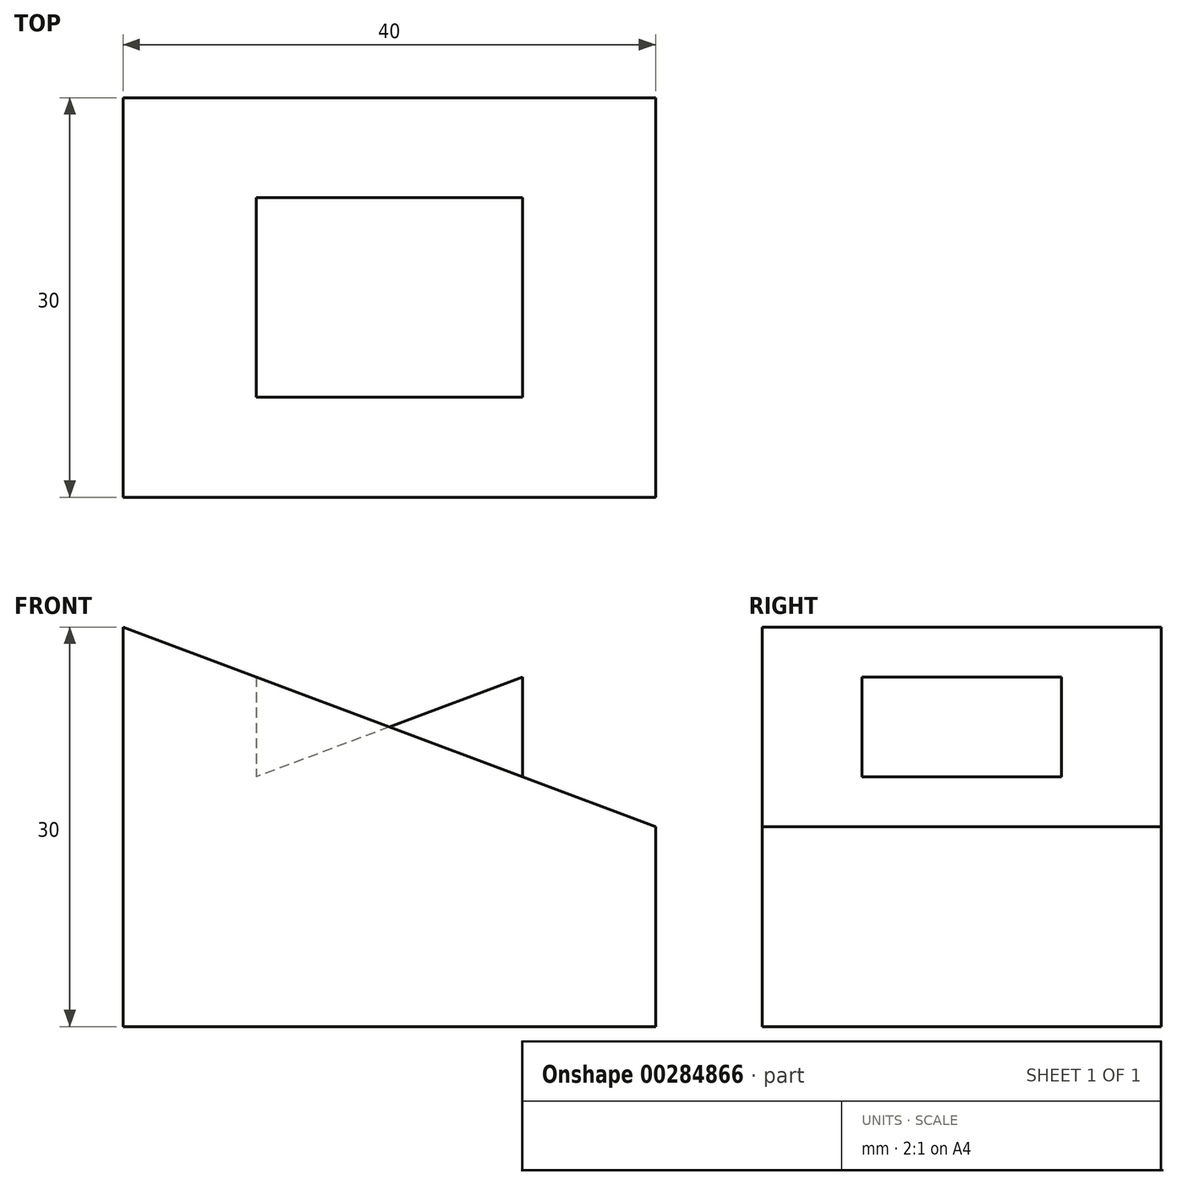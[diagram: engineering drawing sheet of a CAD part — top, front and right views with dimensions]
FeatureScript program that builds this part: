
annotation { "Feature Type Name" : "Feature", "Feature Type Description" : "" }
export const myFeature = defineFeature(function(context is Context, id is Id, definition is map)
    precondition{}
    {
        {
            var Q0;
            Q0=qCreatedBy(makeId("Front.planeOp"),FACE);
            var sketch = newSketch(context, id + "F0", { "sketchPlane" : qUnion([Q0])});
            skLineSegment(sketch, "E0.bottom", {"start": v(0, 0) * mm, "end": v(40, 0) * mm});
            skLineSegment(sketch, "E0.top", {"start": v(0, 30) * mm, "end": v(40, 30) * mm});
            skLineSegment(sketch, "E0.left", {"start": v(0, 0) * mm, "end": v(0, 30) * mm});
            skLineSegment(sketch, "E0.right", {"start": v(40, 0) * mm, "end": v(40, 30) * mm});
            skLineSegment(sketch, "E1", {"start": v(0, 30) * mm, "end": v(40, 15) * mm});
            skLineSegment(sketch, "E2.bottom", {"start": v(10, 26.25) * mm, "end": v(30, 26.25) * mm});
            skLineSegment(sketch, "E2.top", {"start": v(10, 18.75) * mm, "end": v(30, 18.75) * mm});
            skLineSegment(sketch, "E2.left", {"start": v(10, 26.25) * mm, "end": v(10, 18.75) * mm});
            skLineSegment(sketch, "E2.right", {"start": v(30, 26.25) * mm, "end": v(30, 18.75) * mm});
            skLineSegment(sketch, "E3", {"start": v(30, 26.25) * mm, "end": v(10, 18.75) * mm});
            skSolve(sketch);
        }
        {
            var Q0;
            {var subQ4=sQuery(id+"F0.wireOp",EDGE,"E0.bottom");Q0=makeQuery(id+"F0.imprint","IMPRINT",FACE,{"disambiguationData":[TD([[makeQuery(id+"F0.imprint","IMPRINT",EDGE,{"derivedFrom":subQ4}),1.0]])]});}
            var Q1;
            {var subQ2=sQuery(id+"F0.wireOp",EDGE,"E2.top");Q1=makeQuery(id+"F0.imprint","IMPRINT",FACE,{"disambiguationData":[TD([[makeQuery(id+"F0.imprint","IMPRINT",EDGE,{"derivedFrom":subQ2}),1.0]])]});}
            var Q2;
            {var subQ0=sQuery(id+"F0.wireOp",EDGE,"E2.left");Q2=makeQuery(id+"F0.imprint","IMPRINT",FACE,{"disambiguationData":[TD([[makeQuery(id+"F0.imprint","IMPRINT",EDGE,{"derivedFrom":subQ0}),1.0]])]});}
            extrude(context, id + "F1", {"entities" : qUnion([Q0, Q1, Q2]), "depth" : 30 * mm, "symmetric" : true});
        }
        {
            var Q0;
            {var subQ0=sQuery(id+"F0.wireOp",EDGE,"E2.left");Q0=makeQuery(id+"F0.imprint","IMPRINT",FACE,{"disambiguationData":[TD([[makeQuery(id+"F0.imprint","IMPRINT",EDGE,{"derivedFrom":subQ0}),1.0]])]});}
            extrude(context, id + "F2", {"entities" : qUnion([Q0]), "operationType" : NewBodyOperationType.REMOVE, "oppositeDirection" : true, "depth" : 15 * mm, "symmetric" : true});
        }
        {
            var Q0;
            {var subQ0=sQuery(id+"F0.wireOp",EDGE,"E2.right");Q0=makeQuery(id+"F0.imprint","IMPRINT",FACE,{"disambiguationData":[TD([[makeQuery(id+"F0.imprint","IMPRINT",EDGE,{"derivedFrom":subQ0}),-1.0]])]});}
            extrude(context, id + "F3", {"entities" : qUnion([Q0]), "operationType" : NewBodyOperationType.ADD, "depth" : 15 * mm, "symmetric" : true});
        }
    });
